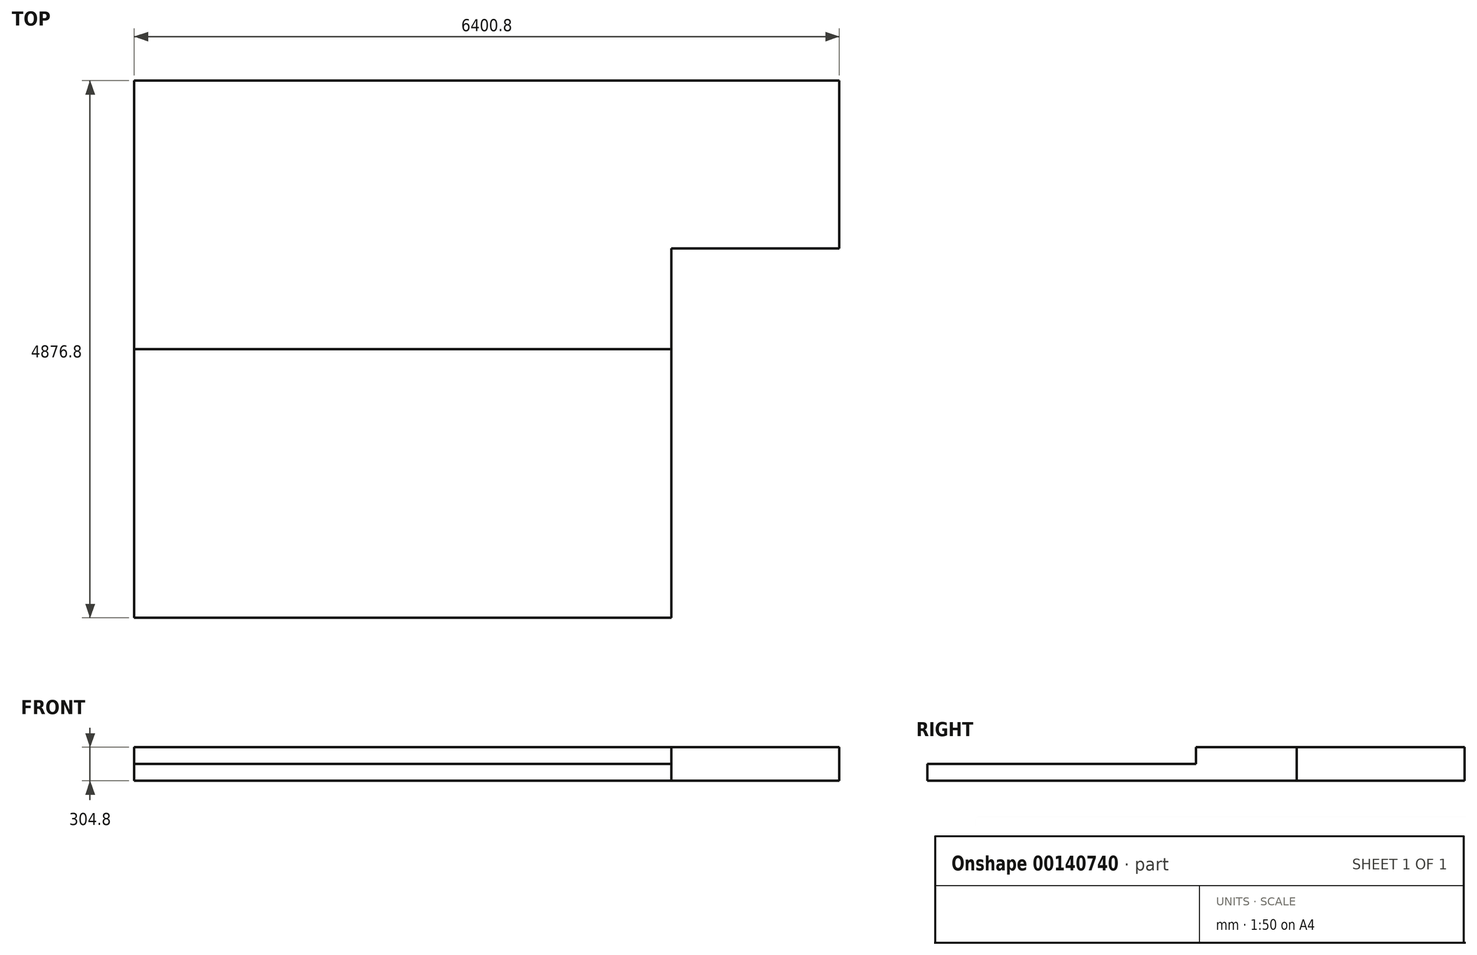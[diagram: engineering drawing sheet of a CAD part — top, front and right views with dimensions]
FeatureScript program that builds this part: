
annotation { "Feature Type Name" : "Feature", "Feature Type Description" : "" }
export const myFeature = defineFeature(function(context is Context, id is Id, definition is map)
    precondition{}
    {
        {
            var Q0;
            Q0=qCreatedBy(makeId("Top.planeOp"),FACE);
            var sketch = newSketch(context, id + "F0", { "sketchPlane" : qUnion([Q0])});
            skLineSegment(sketch, "E0.bottom", {"start": v(2438.4, 2438.4) * mm, "end": v(-2438.4, 2438.4) * mm});
            skLineSegment(sketch, "E0.top", {"start": v(2438.4, -2438.4) * mm, "end": v(-2438.4, -2438.4) * mm});
            skLineSegment(sketch, "E0.left", {"start": v(2438.4, 2438.4) * mm, "end": v(2438.4, -2438.4) * mm});
            skLineSegment(sketch, "E0.right", {"start": v(-2438.4, 2438.4) * mm, "end": v(-2438.4, -2438.4) * mm});
            skPoint(sketch, "E0.middle", {"position": v(0, 0) * mm});
            skLineSegment(sketch, "E1.bottom", {"start": v(2438.4, 2438.4) * mm, "end": v(3962.4, 2438.4) * mm});
            skLineSegment(sketch, "E1.top", {"start": v(2438.4, 914.4) * mm, "end": v(3962.4, 914.4) * mm});
            skLineSegment(sketch, "E1.left", {"start": v(2438.4, 2438.4) * mm, "end": v(2438.4, 914.4) * mm});
            skLineSegment(sketch, "E1.right", {"start": v(3962.4, 2438.4) * mm, "end": v(3962.4, 914.4) * mm});
            skSolve(sketch);
        }
        {
            var Q0;
            Q0 = qSketchRegion(id + "F0", true);
            extrude(context, id + "F1", {"entities" : qUnion([Q0]), "oppositeDirection" : true, "depth" : 304.8 * mm});
        }
        {
            var Q0;
            Q0=makeQuery(id+"F1.opExtrude","CAP_FACE",FACE,{"disambiguationData":[OSD([sQuery(id+"F0.wireOp",EDGE,"E0.bottom"),sQuery(id+"F0.wireOp",EDGE,"E0.top"),sQuery(id+"F0.wireOp",EDGE,"E0.left"),sQuery(id+"F0.wireOp",EDGE,"E0.right"),sQuery(id+"F0.wireOp",EDGE,"E1.bottom"),sQuery(id+"F0.wireOp",EDGE,"E1.top"),sQuery(id+"F0.wireOp",EDGE,"E1.right")])],"isStart":true});
            var sketch = newSketch(context, id + "F2", { "sketchPlane" : qUnion([Q0])});
            skLineSegment(sketch, "E2.bottom", {"start": v(-2438.4, -2438.4) * mm, "end": v(2438.4, -2438.4) * mm});
            skLineSegment(sketch, "E2.top", {"start": v(-2438.4, 0) * mm, "end": v(2438.4, 0) * mm});
            skLineSegment(sketch, "E2.left", {"start": v(-2438.4, -2438.4) * mm, "end": v(-2438.4, 0) * mm});
            skLineSegment(sketch, "E2.right", {"start": v(2438.4, -2438.4) * mm, "end": v(2438.4, 0) * mm});
            skSolve(sketch);
        }
        {
            var Q0;
            Q0=makeQuery(id+"F2.imprint","IMPRINT",FACE,{"disambiguationData":[TD([[makeQuery(id+"F2.imprint","IMPRINT",EDGE,{"derivedFrom":sQuery(id+"F2.wireOp",EDGE,"E2.bottom")}),-1.0]])]});
            extrude(context, id + "F3", {"entities" : qUnion([Q0]), "operationType" : NewBodyOperationType.REMOVE, "oppositeDirection" : true, "depth" : 152.4 * mm});
        }
    });
